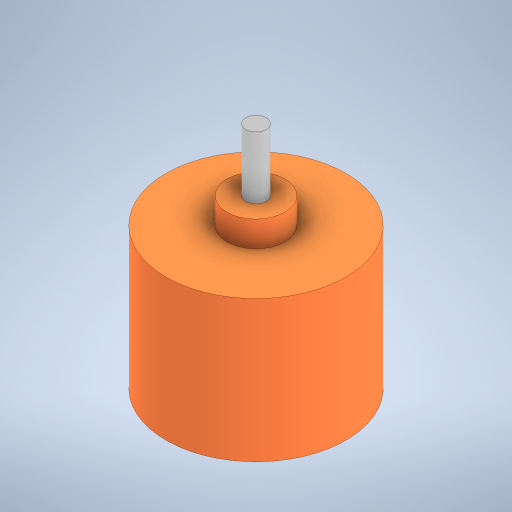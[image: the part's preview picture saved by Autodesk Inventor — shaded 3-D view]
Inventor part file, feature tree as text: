
AUTODESK INVENTOR PART (.ipt)
format: ipt  version: 2024 (Build 280153000, 153)  size: 251,392 bytes
history: native  units: in
note: dims shown in document units (in); Inventor stores cm internally (conversion verified against a paired STEP export)
features: extrude x3, sketch x3
ambient origin geometry x8: Origin, YZ Plane, XZ Plane, XY Plane, X Axis, Y Axis, Z Axis, Center Point
bodies: Solid1 (feature_tree), Solid2 (feature_tree)
feature tree (6):
  extrude  "Extrusion1"  Depth=0.8661in TaperAngle=0.0deg
  extrude  "Extrusion2"  Depth=0.1575in TaperAngle=0.0deg
  extrude  "Extrusion3"  Depth=0.3819in TaperAngle=0.0deg
  sketch  "Sketch1"  dims[d0=1.1024in d1=0.8661in d2=0.0in]
  sketch  "Sketch2"  dims[d3=0.3543in d4=0.1575in d5=0.0in]
  sketch  "Sketch3"  dims[d6=0.126in d7=0.3819in d8=0.0in]
